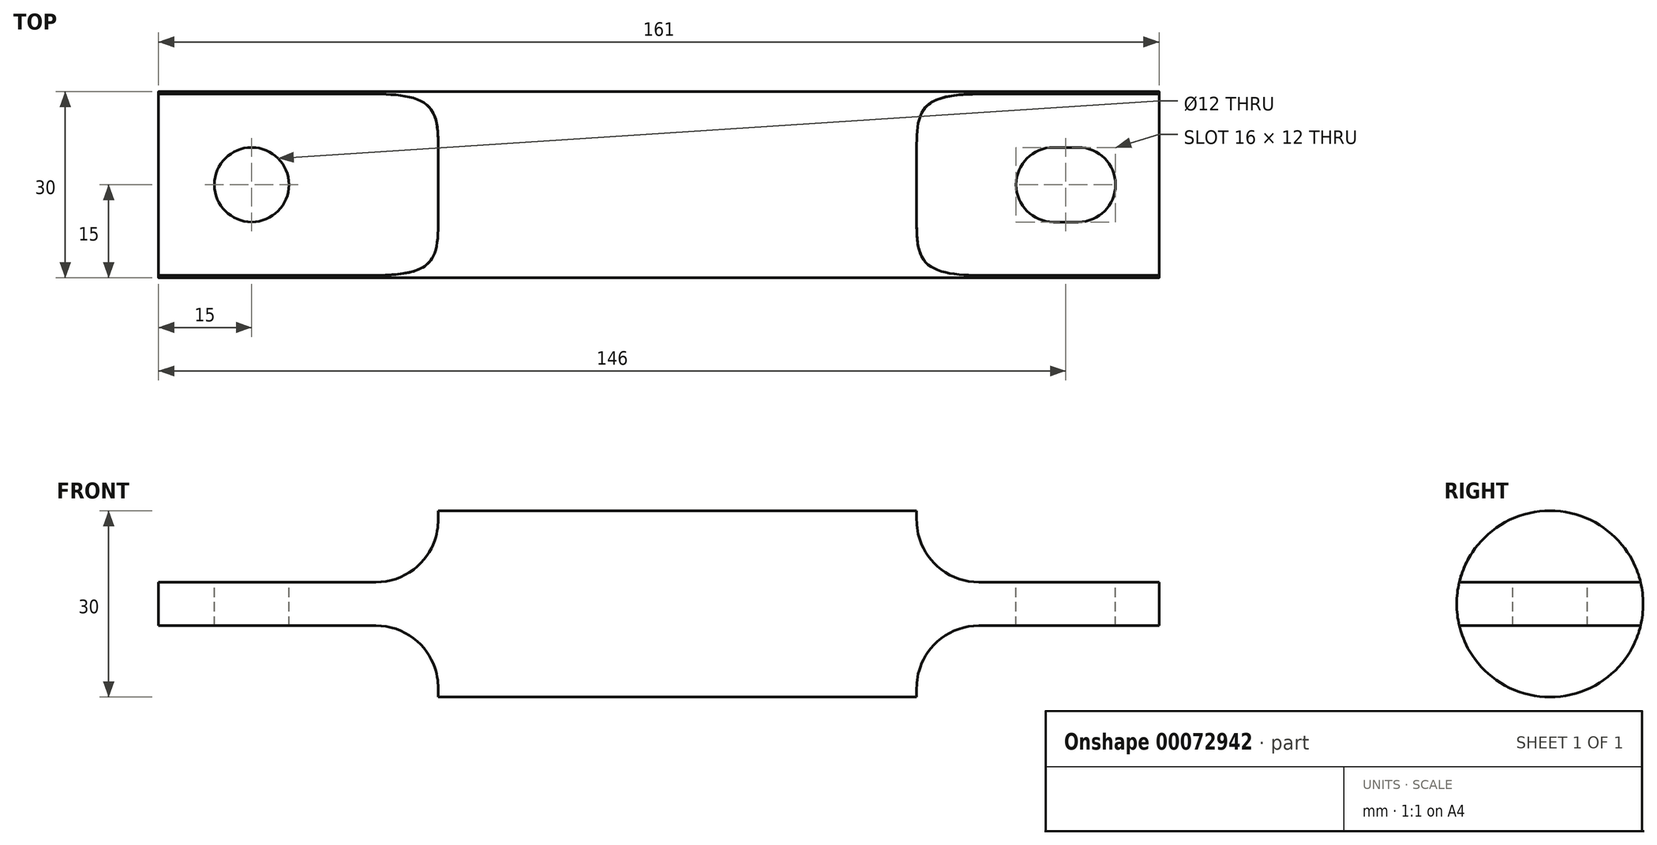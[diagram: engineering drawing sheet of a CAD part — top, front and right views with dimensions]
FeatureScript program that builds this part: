
annotation { "Feature Type Name" : "Feature", "Feature Type Description" : "" }
export const myFeature = defineFeature(function(context is Context, id is Id, definition is map)
    precondition{}
    {
        {
            var Q0;
            Q0=qCreatedBy(makeId("Right.planeOp"),FACE);
            var sketch = newSketch(context, id + "F0", { "sketchPlane" : qUnion([Q0])});
            skCircle(sketch, "E0", {"center": v(0, 0) * mm, "radius": 15 * mm});
            skSolve(sketch);
        }
        {
            var Q0;
            Q0=makeQuery(id+"F0.imprint","IMPRINT",FACE,{"disambiguationData":[TD([[makeQuery(id+"F0.imprint","IMPRINT",EDGE,{"derivedFrom":sQuery(id+"F0.wireOp",EDGE,"E0")}),1.0]])]});
            extrude(context, id + "F1", {"entities" : qUnion([Q0]), "depth" : 161 * mm, "symmetric" : true});
        }
        {
            var Q0;
            Q0=qCreatedBy(makeId("Front.planeOp"),FACE);
            var sketch = newSketch(context, id + "F2", { "sketchPlane" : qUnion([Q0])});
            skLineSegment(sketch, "E1.bottom", {"start": v(-80.5, 15) * mm, "end": v(-35.5, 15) * mm});
            skLineSegment(sketch, "E1.top", {"start": v(-80.5, 3.5) * mm, "end": v(-35.5, 3.5) * mm});
            skLineSegment(sketch, "E1.left", {"start": v(-80.5, 15) * mm, "end": v(-80.5, 3.5) * mm});
            skLineSegment(sketch, "E1.right", {"start": v(-35.5, 15) * mm, "end": v(-35.5, 3.5) * mm});
            skLineSegment(sketch, "E2", {"start": v(-117.46, 0) * mm, "end": v(110.21, 0) * mm, "construction": true});
            skLineSegment(sketch, "E3.MirrorCS", {"start": v(-35.5, -15) * mm, "end": v(-35.5, -3.5) * mm});
            skLineSegment(sketch, "E4.MirrorCS", {"start": v(-80.5, -3.5) * mm, "end": v(-35.5, -3.5) * mm});
            skLineSegment(sketch, "E5.MirrorCS", {"start": v(-80.5, -15) * mm, "end": v(-80.5, -3.5) * mm});
            skLineSegment(sketch, "E6.MirrorCS", {"start": v(-80.5, -15) * mm, "end": v(-35.5, -15) * mm});
            skLineSegment(sketch, "E7.bottom", {"start": v(80.5, 15) * mm, "end": v(41.5, 15) * mm});
            skLineSegment(sketch, "E7.top", {"start": v(80.5, 3.5) * mm, "end": v(41.5, 3.5) * mm});
            skLineSegment(sketch, "E7.left", {"start": v(80.5, 15) * mm, "end": v(80.5, 3.5) * mm});
            skLineSegment(sketch, "E7.right", {"start": v(41.5, 15) * mm, "end": v(41.5, 3.5) * mm});
            skLineSegment(sketch, "E8.MirrorCS", {"start": v(80.5, -15) * mm, "end": v(80.5, -3.5) * mm});
            skLineSegment(sketch, "E9.MirrorCS", {"start": v(80.5, -15) * mm, "end": v(41.5, -15) * mm});
            skLineSegment(sketch, "E10.MirrorCS", {"start": v(41.5, -15) * mm, "end": v(41.5, -3.5) * mm});
            skLineSegment(sketch, "E11.MirrorCS", {"start": v(80.5, -3.5) * mm, "end": v(41.5, -3.5) * mm});
            skSolve(sketch);
        }
        {
            var Q0;
            Q0=qSketchRegion(id+"F2",true);
            extrude(context, id + "F3", {"entities" : qUnion([Q0]), "operationType" : NewBodyOperationType.REMOVE, "oppositeDirection" : true, "depth" : 30 * mm, "symmetric" : true});
        }
        {
            var Q0;
            Q0=makeQuery(id+"F3.boolean.opBoolean","COPY",EDGE,{"derivedFrom":makeQuery(id+"F3.opExtrude","SWEPT_EDGE",EDGE,{"disambiguationData":[OSD([sQuery(id+"F2.wireOp",EDGE,"E7.top"),sQuery(id+"F2.wireOp",EDGE,"E7.right")])]})});
            var Q1;
            Q1=makeQuery(id+"F3.boolean.opBoolean","COPY",EDGE,{"derivedFrom":makeQuery(id+"F3.opExtrude","SWEPT_EDGE",EDGE,{"disambiguationData":[OSD([sQuery(id+"F2.wireOp",EDGE,"E1.top"),sQuery(id+"F2.wireOp",EDGE,"E1.right")])]})});
            var Q2;
            Q2=makeQuery(id+"F3.boolean.opBoolean","COPY",EDGE,{"derivedFrom":makeQuery(id+"F3.opExtrude","SWEPT_EDGE",EDGE,{"disambiguationData":[OSD([sQuery(id+"F2.wireOp",EDGE,"E10.MirrorCS"),sQuery(id+"F2.wireOp",EDGE,"E11.MirrorCS")])]})});
            var Q3;
            Q3=makeQuery(id+"F3.boolean.opBoolean","COPY",EDGE,{"derivedFrom":makeQuery(id+"F3.opExtrude","SWEPT_EDGE",EDGE,{"disambiguationData":[OSD([sQuery(id+"F2.wireOp",EDGE,"E3.MirrorCS"),sQuery(id+"F2.wireOp",EDGE,"E4.MirrorCS")])]})});
            fillet(context, id + "F4", {"entities" : qUnion([Q0, Q1, Q2, Q3]), "radius" : 10 * mm, "tangentPropagation" : true, "allowEdgeOverflow" : false});
        }
        {
            var Q0;
            Q0=qCreatedBy(makeId("Top.planeOp"),FACE);
            var sketch = newSketch(context, id + "F5", { "sketchPlane" : qUnion([Q0])});
            skCircle(sketch, "E12", {"center": v(-65.5, 0) * mm, "radius": 6 * mm});
            skArc(sketch, "E13", {"start": v(63.5, 6) * mm, "mid": v(57.5, 0) * mm, "end": v(63.5, -6) * mm});
            skArc(sketch, "E14", {"start": v(67.5, -6) * mm, "mid": v(73.5, 0) * mm, "end": v(67.5, 6) * mm});
            skLineSegment(sketch, "E15", {"start": v(63.5, 6) * mm, "end": v(67.5, 6) * mm});
            skLineSegment(sketch, "E16", {"start": v(63.5, -6) * mm, "end": v(67.5, -6) * mm});
            skSolve(sketch);
        }
        {
            var Q0;
            Q0=qSketchRegion(id+"F5",true);
            extrude(context, id + "F6", {"entities" : qUnion([Q0]), "operationType" : NewBodyOperationType.REMOVE, "oppositeDirection" : true, "depth" : 7 * mm, "symmetric" : true});
        }
    });
